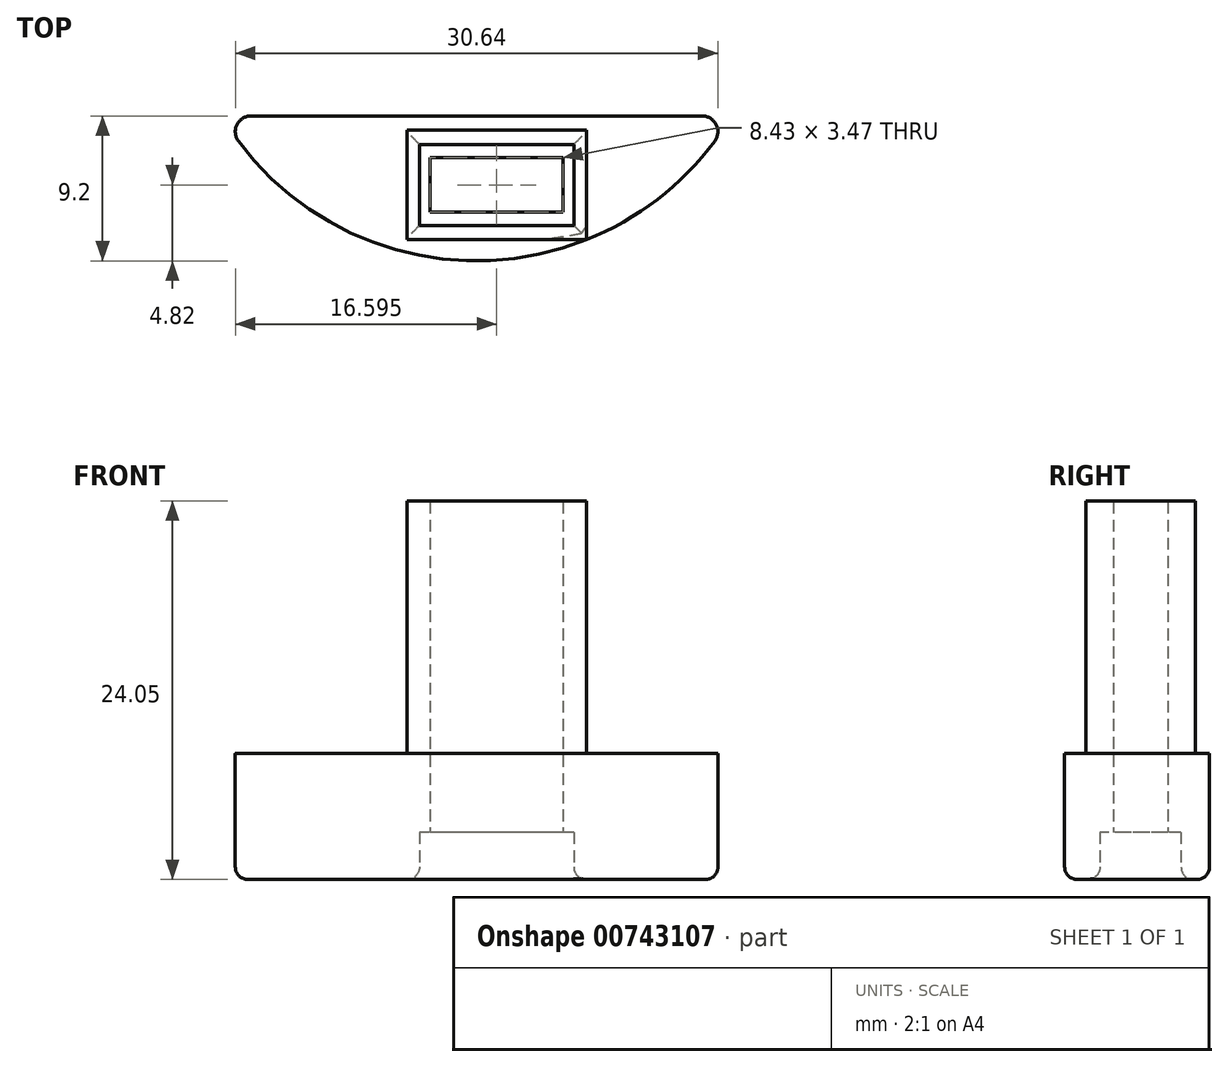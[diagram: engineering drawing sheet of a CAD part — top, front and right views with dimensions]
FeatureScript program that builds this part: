
annotation { "Feature Type Name" : "Feature", "Feature Type Description" : "" }
export const myFeature = defineFeature(function(context is Context, id is Id, definition is map)
    precondition{}
    {
        {
            var Q0;
            Q0=qCreatedBy(makeId("Top.planeOp"),FACE);
            var sketch = newSketch(context, id + "F0", { "sketchPlane" : qUnion([Q0])});
            skCircle(sketch, "E0", {"center": v(0, 0) * mm, "radius": 18.85 * mm});
            skLineSegment(sketch, "E1.bottom", {"start": v(0, 0) * mm, "end": v(1.27, 0) * mm});
            skLineSegment(sketch, "E1.top", {"start": v(0, -14.03) * mm, "end": v(1.28, -14.03) * mm});
            skLineSegment(sketch, "E1.left", {"start": v(0, 0) * mm, "end": v(0, -14.03) * mm});
            skLineSegment(sketch, "E1.right", {"start": v(1.27, 0) * mm, "end": v(1.28, -14.03) * mm});
            skLineSegment(sketch, "E2.bottom", {"start": v(6.18, -11.46) * mm, "end": v(-3.62, -11.46) * mm});
            skLineSegment(sketch, "E2.top", {"start": v(6.18, -16.6) * mm, "end": v(-3.62, -16.6) * mm});
            skLineSegment(sketch, "E2.left", {"start": v(6.18, -11.45) * mm, "end": v(6.18, -16.6) * mm});
            skLineSegment(sketch, "E2.right", {"start": v(-3.62, -11.46) * mm, "end": v(-3.62, -16.6) * mm});
            skPoint(sketch, "E2.middle", {"position": v(1.28, -14.03) * mm});
            skLineSegment(sketch, "E3", {"start": v(0, -18.85) * mm, "end": v(0, -9.65) * mm, "construction": true});
            skLineSegment(sketch, "E4", {"start": v(16.2, -9.65) * mm, "end": v(-16.2, -9.65) * mm});
            skLineSegment(sketch, "E5.bottom", {"start": v(6.97, -17.51) * mm, "end": v(-4.42, -17.51) * mm});
            skLineSegment(sketch, "E5.top", {"start": v(6.97, -10.55) * mm, "end": v(-4.42, -10.55) * mm});
            skLineSegment(sketch, "E5.left", {"start": v(6.97, -17.51) * mm, "end": v(6.97, -10.55) * mm});
            skLineSegment(sketch, "E5.right", {"start": v(-4.42, -17.51) * mm, "end": v(-4.42, -10.55) * mm});
            skLineSegment(sketch, "E6.bottom", {"start": v(5.5, -12.3) * mm, "end": v(-2.94, -12.3) * mm});
            skLineSegment(sketch, "E6.top", {"start": v(5.5, -15.76) * mm, "end": v(-2.94, -15.76) * mm});
            skLineSegment(sketch, "E6.left", {"start": v(5.5, -12.3) * mm, "end": v(5.5, -15.76) * mm});
            skLineSegment(sketch, "E6.right", {"start": v(-2.94, -12.3) * mm, "end": v(-2.94, -15.76) * mm});
            skSolve(sketch);
        }
        {
            var Q0;
            {var subQ0=sQuery(id+"F0.wireOp",EDGE,"E5.bottom");Q0=makeQuery(id+"F0.imprint","IMPRINT",FACE,{"disambiguationData":[TD([[makeQuery(id+"F0.imprint","IMPRINT",EDGE,{"derivedFrom":subQ0}),1.0]])]});}
            var Q1;
            {var subQ0=sQuery(id+"F0.wireOp",EDGE,"E5.left");Q1=makeQuery(id+"F0.imprint","IMPRINT",FACE,{"disambiguationData":[TD([[makeQuery(id+"F0.imprint","IMPRINT",EDGE,{"derivedFrom":subQ0}),-1.0]])]});}
            var Q2;
            {var subQ0=sQuery(id+"F0.wireOp",EDGE,"E4");var subQ1=sQuery(id+"F0.wireOp",EDGE,"E1.left");var subQ2=makeQuery(id+"F0.imprint","INTERSECT",VERTEX,{"derivedFrom":[subQ1,subQ0]});Q2=makeQuery(id+"F0.imprint","IMPRINT",FACE,{"disambiguationData":[TD([[makeQuery(id+"F0.imprint","IMPRINT",EDGE,{"disambiguationData":[TD([[subQ2,-1.0]])],"derivedFrom":subQ1}),1.0]])]});}
            var Q3;
            Q3=makeQuery(id+"F0.imprint","IMPRINT",FACE,{"disambiguationData":[TD([[makeQuery(id+"F0.imprint","IMPRINT",EDGE,{"derivedFrom":sQuery(id+"F0.wireOp",EDGE,"E2.top")}),1.0]])]});
            var Q4;
            {var subQ0=sQuery(id+"F0.wireOp",EDGE,"E5.top");var subQ1=sQuery(id+"F0.wireOp",EDGE,"E1.left");var subQ2=makeQuery(id+"F0.imprint","INTERSECT",VERTEX,{"derivedFrom":[subQ1,subQ0]});Q4=makeQuery(id+"F0.imprint","IMPRINT",FACE,{"disambiguationData":[TD([[makeQuery(id+"F0.imprint","IMPRINT",EDGE,{"disambiguationData":[TD([[subQ2,-1.0]])],"derivedFrom":subQ1}),1.0]])]});}
            var Q5;
            Q5=makeQuery(id+"F0.imprint","IMPRINT",FACE,{"disambiguationData":[TD([[makeQuery(id+"F0.imprint","IMPRINT",EDGE,{"derivedFrom":sQuery(id+"F0.wireOp",EDGE,"E2.top")}),-1.0]])]});
            var Q6;
            {var subQ0=sQuery(id+"F0.wireOp",EDGE,"E2.bottom");var subQ1=sQuery(id+"F0.wireOp",EDGE,"E1.left");var subQ2=makeQuery(id+"F0.imprint","INTERSECT",VERTEX,{"derivedFrom":[subQ1,subQ0]});Q6=makeQuery(id+"F0.imprint","IMPRINT",FACE,{"disambiguationData":[TD([[makeQuery(id+"F0.imprint","IMPRINT",EDGE,{"disambiguationData":[TD([[subQ2,-1.0]])],"derivedFrom":subQ1}),1.0]])]});}
            extrude(context, id + "F1", {"entities" : qUnion([Q0, Q1, Q2, Q3, Q4, Q5, Q6]), "depth" : 8 * mm, "offsetDistance" : 25 * mm});
        }
        {
            var Q0;
            Q0=makeQuery(id+"F0.imprint","IMPRINT",FACE,{"disambiguationData":[TD([[makeQuery(id+"F0.imprint","IMPRINT",EDGE,{"derivedFrom":sQuery(id+"F0.wireOp",EDGE,"E2.top")}),-1.0]])]});
            var Q1;
            {var subQ0=sQuery(id+"F0.wireOp",EDGE,"E2.bottom");var subQ1=sQuery(id+"F0.wireOp",EDGE,"E1.left");var subQ2=makeQuery(id+"F0.imprint","INTERSECT",VERTEX,{"derivedFrom":[subQ1,subQ0]});Q1=makeQuery(id+"F0.imprint","IMPRINT",FACE,{"disambiguationData":[TD([[makeQuery(id+"F0.imprint","IMPRINT",EDGE,{"disambiguationData":[TD([[subQ2,-1.0]])],"derivedFrom":subQ1}),1.0]])]});}
            extrude(context, id + "F2", {"entities" : qUnion([Q0, Q1]), "operationType" : NewBodyOperationType.REMOVE, "depth" : 3 * mm, "offsetDistance" : 25 * mm});
        }
        {
            var Q0;
            Q0=makeQuery(id+"F2.boolean.opBoolean","COPY",FACE,{"derivedFrom":makeQuery(id+"F2.opExtrude","CAP_FACE",FACE,{"disambiguationData":[OSD([sQuery(id+"F0.wireOp",EDGE,"E2.bottom"),sQuery(id+"F0.wireOp",EDGE,"E2.top"),sQuery(id+"F0.wireOp",EDGE,"E2.left"),sQuery(id+"F0.wireOp",EDGE,"E2.right"),sQuery(id+"F0.wireOp",EDGE,"E6.bottom"),sQuery(id+"F0.wireOp",EDGE,"E6.top"),sQuery(id+"F0.wireOp",EDGE,"E6.left"),sQuery(id+"F0.wireOp",EDGE,"E6.right")])],"isStart":false})});
            extrude(context, id + "F3", {"entities" : qUnion([Q0]), "operationType" : NewBodyOperationType.ADD, "oppositeDirection" : true, "depth" : 21 * mm, "offsetDistance" : 25 * mm});
        }
        {
            var Q0;
            Q0=makeQuery(id+"F0.imprint","IMPRINT",FACE,{"disambiguationData":[TD([[makeQuery(id+"F0.imprint","IMPRINT",EDGE,{"derivedFrom":sQuery(id+"F0.wireOp",EDGE,"E2.top")}),1.0]])]});
            var Q1;
            {var subQ0=sQuery(id+"F0.wireOp",EDGE,"E5.top");var subQ1=sQuery(id+"F0.wireOp",EDGE,"E1.left");var subQ2=makeQuery(id+"F0.imprint","INTERSECT",VERTEX,{"derivedFrom":[subQ1,subQ0]});Q1=makeQuery(id+"F0.imprint","IMPRINT",FACE,{"disambiguationData":[TD([[makeQuery(id+"F0.imprint","IMPRINT",EDGE,{"disambiguationData":[TD([[subQ2,-1.0]])],"derivedFrom":subQ1}),1.0]])]});}
            extrude(context, id + "F4", {"entities" : qUnion([Q0, Q1]), "operationType" : NewBodyOperationType.ADD, "depth" : 24.05 * mm, "offsetDistance" : 25 * mm});
        }
        {
            var Q0;
            {var subQ0=sQuery(id+"F0.wireOp",EDGE,"E4");var subQ1=sQuery(id+"F0.wireOp",EDGE,"E0");Q0=makeQuery(id+"F1.opExtrude","SWEPT_EDGE",EDGE,{"disambiguationData":[OSD([subQ1,subQ0]),TDD([makeQuery(id+"F0.imprint","INTERSECT",VERTEX,{"disambiguationData":[OD(0.0)],"derivedFrom":[subQ1,subQ0]})])]});}
            var Q1;
            {var subQ0=sQuery(id+"F0.wireOp",EDGE,"E4");var subQ1=sQuery(id+"F0.wireOp",EDGE,"E0");Q1=makeQuery(id+"F1.opExtrude","SWEPT_EDGE",EDGE,{"disambiguationData":[OSD([subQ1,subQ0]),TDD([makeQuery(id+"F0.imprint","INTERSECT",VERTEX,{"disambiguationData":[OD(1.0)],"derivedFrom":[subQ1,subQ0]})])]});}
            fillet(context, id + "F5", {"entities" : qUnion([Q0, Q1]), "radius" : 1 * mm, "tangentPropagation" : true, "allowEdgeOverflow" : false});
        }
        {
            var Q0;
            Q0=makeQuery(id+"F1.opExtrude","CAP_FACE",FACE,{"disambiguationData":[OSD([sQuery(id+"F0.wireOp",EDGE,"E0"),sQuery(id+"F0.wireOp",EDGE,"E4"),sQuery(id+"F0.wireOp",EDGE,"E6.bottom"),sQuery(id+"F0.wireOp",EDGE,"E6.top"),sQuery(id+"F0.wireOp",EDGE,"E6.left"),sQuery(id+"F0.wireOp",EDGE,"E6.right")])],"isStart":true});
            fillet(context, id + "F6", {"entities" : qUnion([Q0]), "radius" : .8 * mm, "tangentPropagation" : true, "allowEdgeOverflow" : false});
        }
    });
